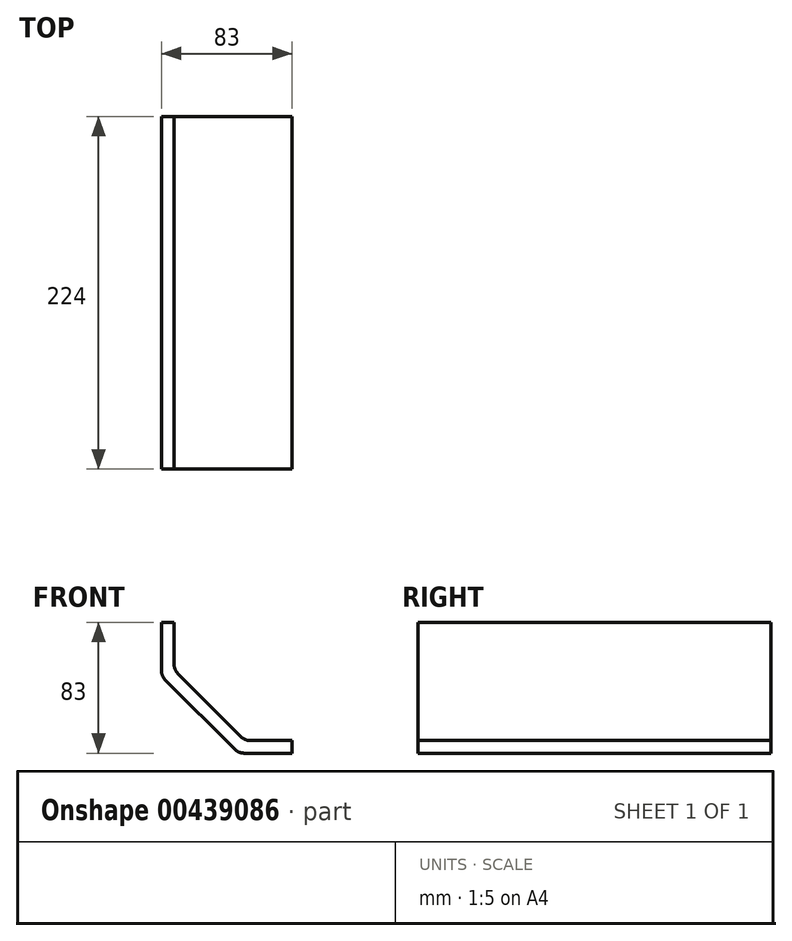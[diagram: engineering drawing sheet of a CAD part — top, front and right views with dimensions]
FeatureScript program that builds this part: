
annotation { "Feature Type Name" : "Feature", "Feature Type Description" : "" }
export const myFeature = defineFeature(function(context is Context, id is Id, definition is map)
    precondition{}
    {
        {
            var Q0;
            Q0=qCreatedBy(makeId("Front.planeOp"),FACE);
            var sketch = newSketch(context, id + "F0", { "sketchPlane" : qUnion([Q0])});
            skLineSegment(sketch, "E0.bottom", {"start": v(-24.86, 54.17) * mm, "end": v(-16.86, 54.17) * mm});
            skLineSegment(sketch, "E0.top", {"start": v(-24.86, 24.17) * mm, "end": v(-16.86, 24.17) * mm});
            skLineSegment(sketch, "E0.left", {"start": v(-24.86, 54.17) * mm, "end": v(-24.86, 24.17) * mm});
            skLineSegment(sketch, "E0.right", {"start": v(-16.86, 54.17) * mm, "end": v(-16.86, 24.17) * mm});
            skLineSegment(sketch, "E1.left", {"start": v(-24.86, 24.17) * mm, "end": v(-24.86, 20.17) * mm});
            skLineSegment(sketch, "E2", {"start": v(-24.86, 20.17) * mm, "end": v(-16.86, 24.17) * mm});
            skLineSegment(sketch, "E3.bottom", {"start": v(28.14, -20.83) * mm, "end": v(58.14, -20.83) * mm});
            skLineSegment(sketch, "E3.top", {"start": v(28.14, -28.83) * mm, "end": v(58.14, -28.83) * mm});
            skLineSegment(sketch, "E3.left", {"start": v(28.14, -20.83) * mm, "end": v(28.14, -28.83) * mm});
            skLineSegment(sketch, "E3.right", {"start": v(58.14, -20.83) * mm, "end": v(58.14, -28.83) * mm});
            skLineSegment(sketch, "E4.top", {"start": v(28.14, -28.83) * mm, "end": v(24.14, -28.83) * mm});
            skLineSegment(sketch, "E5", {"start": v(24.14, -28.83) * mm, "end": v(28.14, -20.83) * mm});
            skLineSegment(sketch, "E6", {"start": v(-16.86, 24.17) * mm, "end": v(28.14, -20.83) * mm});
            skLineSegment(sketch, "E7", {"start": v(-24.86, 20.17) * mm, "end": v(24.14, -28.83) * mm});
            skSolve(sketch);
        }
        {
            var Q0;
            Q0 = qSketchRegion(id + "F0", true);
            extrude(context, id + "F1", {"entities" : qUnion([Q0]), "depth" : 224 * mm});
        }
        {
            var Q0;
            Q0=makeQuery(id+"F1.opExtrude","SWEPT_EDGE",EDGE,{"disambiguationData":[OSD([sQuery(id+"F0.wireOp",EDGE,"E0.right"),sQuery(id+"F0.wireOp",EDGE,"E1.bottom"),sQuery(id+"F0.wireOp",EDGE,"E2"),sQuery(id+"F0.wireOp",EDGE,"E6")])]});
            var Q1;
            Q1=makeQuery(id+"F1.opExtrude","SWEPT_EDGE",EDGE,{"disambiguationData":[OSD([sQuery(id+"F0.wireOp",EDGE,"E3.bottom"),sQuery(id+"F0.wireOp",EDGE,"E3.left"),sQuery(id+"F0.wireOp",EDGE,"E5"),sQuery(id+"F0.wireOp",EDGE,"E6")])]});
            fillet(context, id + "F2", {"entities" : qUnion([Q0, Q1]), "radius" : 8 * mm, "tangentPropagation" : true, "allowEdgeOverflow" : false});
        }
        {
            var Q0;
            Q0=makeQuery(id+"F1.opExtrude","SWEPT_EDGE",EDGE,{"disambiguationData":[OSD([sQuery(id+"F0.wireOp",EDGE,"E1.left"),sQuery(id+"F0.wireOp",EDGE,"E2"),sQuery(id+"F0.wireOp",EDGE,"E7")])]});
            var Q1;
            Q1=makeQuery(id+"F1.opExtrude","SWEPT_EDGE",EDGE,{"disambiguationData":[OSD([sQuery(id+"F0.wireOp",EDGE,"E4.top"),sQuery(id+"F0.wireOp",EDGE,"E5"),sQuery(id+"F0.wireOp",EDGE,"E7")])]});
            fillet(context, id + "F3", {"entities" : qUnion([Q0, Q1]), "radius" : 8 * mm, "tangentPropagation" : true, "allowEdgeOverflow" : false});
        }
    });
